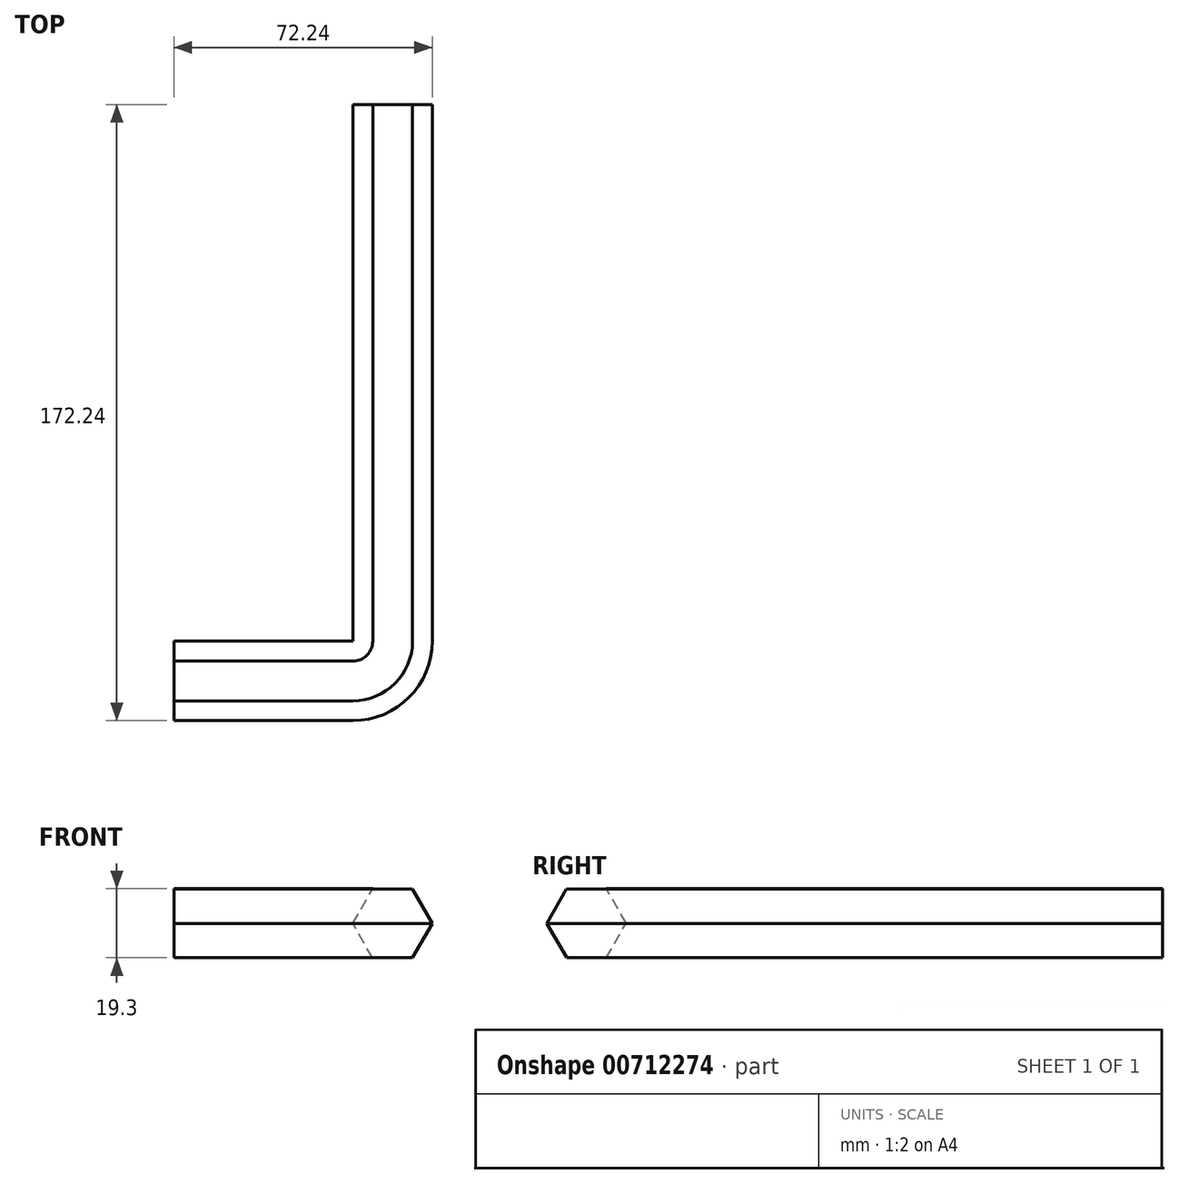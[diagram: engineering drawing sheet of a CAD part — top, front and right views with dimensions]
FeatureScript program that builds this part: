
annotation { "Feature Type Name" : "Feature", "Feature Type Description" : "" }
export const myFeature = defineFeature(function(context is Context, id is Id, definition is map)
    precondition{}
    {
        {
            var Q0;
            Q0=qCreatedBy(makeId("Front.planeOp"),FACE);
            var sketch = newSketch(context, id + "F0", { "sketchPlane" : qUnion([Q0])});
            skCircle(sketch, "E0.cCircle", {"center": v(17.44, 0) * mm, "radius": 9.63 * mm, "construction": true});
            skLineSegment(sketch, "E0.0", {"start": v(28.56, -0.03) * mm, "end": v(22.97, -9.65) * mm});
            skLineSegment(sketch, "E0.1", {"start": v(22.97, -9.65) * mm, "end": v(11.85, -9.61) * mm});
            skLineSegment(sketch, "E0.2", {"start": v(11.85, -9.61) * mm, "end": v(6.32, 0.03) * mm});
            skLineSegment(sketch, "E0.3", {"start": v(6.32, 0.03) * mm, "end": v(11.9, 9.65) * mm});
            skLineSegment(sketch, "E0.4", {"start": v(11.9, 9.65) * mm, "end": v(23.03, 9.61) * mm});
            skLineSegment(sketch, "E0.5", {"start": v(23.03, 9.61) * mm, "end": v(28.56, -0.03) * mm});
            skSolve(sketch);
        }
        {
            var Q0;
            Q0=makeQuery(id+"F0.imprint","IMPRINT",FACE,{"disambiguationData":[TD([[makeQuery(id+"F0.imprint","IMPRINT",EDGE,{"derivedFrom":sQuery(id+"F0.wireOp",EDGE,"E0.0")}),-1.0]])]});
            extrude(context, id + "F1", {"entities" : qUnion([Q0]), "depth" : 150 * mm, "offsetDistance" : 25 * mm});
        }
        {
            var Q0;
            Q0=makeQuery(id+"F1.opExtrude","CAP_FACE",FACE,{"disambiguationData":[OSD([sQuery(id+"F0.wireOp",EDGE,"E0.0"),sQuery(id+"F0.wireOp",EDGE,"E0.1"),sQuery(id+"F0.wireOp",EDGE,"E0.2"),sQuery(id+"F0.wireOp",EDGE,"E0.3"),sQuery(id+"F0.wireOp",EDGE,"E0.4"),sQuery(id+"F0.wireOp",EDGE,"E0.5")])],"isStart":false});
            var sketch = newSketch(context, id + "F2", { "sketchPlane" : qUnion([Q0])});
            skLineSegment(sketch, "E1", {"start": v(6.32, 0.03) * mm, "end": v(6.32, 29.84) * mm});
            skSolve(sketch);
        }
        {
            var Q0;
            Q0=makeQuery(id+"F2.imprint","IMPRINT",FACE,{"disambiguationData":[TD([[makeQuery(id+"F2.imprint","IMPRINT",EDGE,{"derivedFrom":makeQuery(id+"F1.opExtrude","CAP_EDGE",EDGE,{"disambiguationData":[OSD([sQuery(id+"F0.wireOp",EDGE,"E0.0")])],"isStart":false})}),-1.0]])]});
            var Q1;
            Q1=sQuery(id+"F2.wireOp",EDGE,"E1");
            revolve(context, id + "F3", {"operationType" : NewBodyOperationType.ADD, "surfaceOperationType" : NewSurfaceOperationType.NEW, "entities" : qUnion([Q0]), "axis" : qUnion([Q1]), "revolveType" : RevolveType.ONE_DIRECTION, "oppositeDirection" : true, "angle" : 90 * degree});
        }
        {
            var Q0;
            Q0=makeQuery(id+"F3.opRevolve","CAP_FACE",FACE,{"disambiguationData":[OSD([sQuery(id+"F0.wireOp",EDGE,"E0.0"),sQuery(id+"F0.wireOp",EDGE,"E0.1"),sQuery(id+"F0.wireOp",EDGE,"E0.2"),sQuery(id+"F0.wireOp",EDGE,"E0.3"),sQuery(id+"F0.wireOp",EDGE,"E0.4"),sQuery(id+"F0.wireOp",EDGE,"E0.5")])],"isStart":false});
            extrude(context, id + "F4", {"entities" : qUnion([Q0]), "operationType" : NewBodyOperationType.ADD, "depth" : 50 * mm, "offsetDistance" : 25 * mm});
        }
    });
